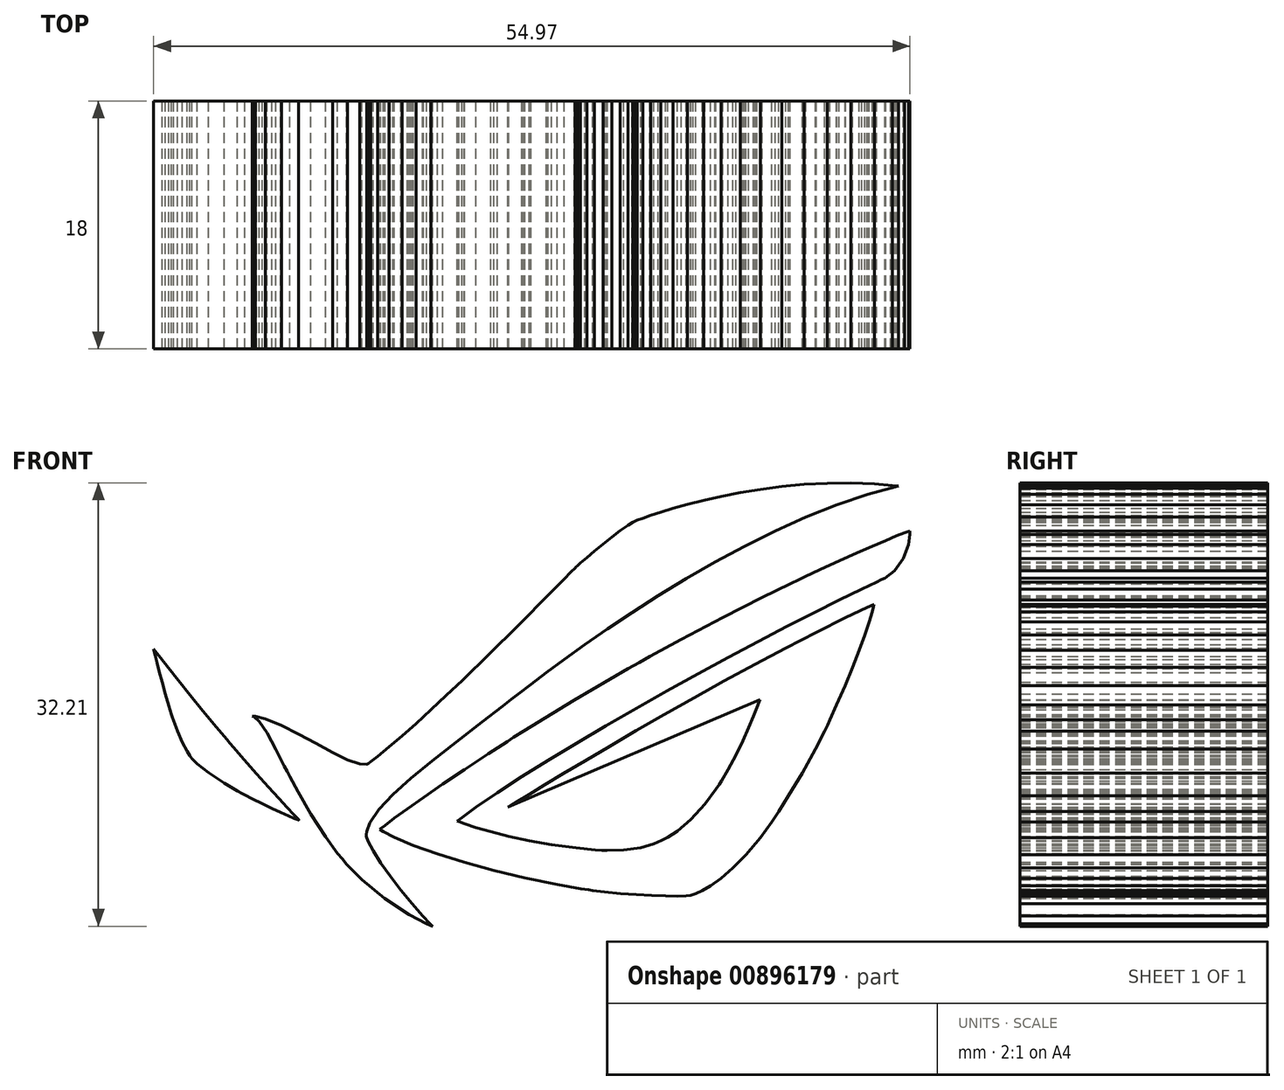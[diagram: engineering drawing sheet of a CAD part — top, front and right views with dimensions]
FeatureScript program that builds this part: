
annotation { "Feature Type Name" : "Feature", "Feature Type Description" : "" }
export const myFeature = defineFeature(function(context is Context, id is Id, definition is map)
    precondition{}
    {
        {
            var Q0;
            Q0=qCreatedBy(makeId("Front.planeOp"),FACE);
            var sketch = newSketch(context, id + "F0", { "sketchPlane" : qUnion([Q0])});
            skLineSegment(sketch, "E0", {"start": v(-0.13, -0.24) * mm, "end": v(-0.06, -0.2) * mm});
            skLineSegment(sketch, "E1", {"start": v(-0.06, -0.2) * mm, "end": v(0.3, 0.03) * mm});
            skLineSegment(sketch, "E2", {"start": v(0.3, 0.03) * mm, "end": v(0.7, 0.26) * mm});
            skLineSegment(sketch, "E3", {"start": v(0.7, 0.26) * mm, "end": v(0.78, 0.3) * mm});
            skLineSegment(sketch, "E4", {"start": v(0.78, 0.3) * mm, "end": v(0.86, 0.35) * mm});
            skLineSegment(sketch, "E5", {"start": v(0.86, 0.35) * mm, "end": v(1.09, 0.48) * mm});
            skLineSegment(sketch, "E6", {"start": v(1.09, 0.48) * mm, "end": v(1.39, 0.63) * mm});
            skLineSegment(sketch, "E7", {"start": v(1.39, 0.63) * mm, "end": v(1.68, 0.78) * mm});
            skLineSegment(sketch, "E8", {"start": v(1.68, 0.78) * mm, "end": v(1.88, 0.88) * mm});
            skLineSegment(sketch, "E9", {"start": v(1.88, 0.88) * mm, "end": v(1.94, 0.91) * mm});
            skLineSegment(sketch, "E10", {"start": v(1.94, 0.91) * mm, "end": v(1.98, 0.93) * mm});
            skLineSegment(sketch, "E11", {"start": v(1.98, 0.93) * mm, "end": v(2.1, 0.98) * mm});
            skLineSegment(sketch, "E12", {"start": v(2.1, 0.98) * mm, "end": v(2.23, 1.05) * mm});
            skLineSegment(sketch, "E13", {"start": v(2.23, 1.05) * mm, "end": v(2.36, 1.1) * mm});
            skLineSegment(sketch, "E14", {"start": v(2.36, 1.1) * mm, "end": v(2.47, 1.15) * mm});
            skLineSegment(sketch, "E15", {"start": v(2.47, 1.15) * mm, "end": v(2.57, 1.2) * mm});
            skLineSegment(sketch, "E16", {"start": v(2.57, 1.2) * mm, "end": v(2.65, 1.23) * mm});
            skLineSegment(sketch, "E17", {"start": v(2.65, 1.23) * mm, "end": v(2.7, 1.25) * mm});
            skLineSegment(sketch, "E18", {"start": v(2.7, 1.25) * mm, "end": v(2.74, 1.26) * mm});
            skLineSegment(sketch, "E19", {"start": v(2.74, 1.26) * mm, "end": v(2.75, 1.26) * mm});
            skLineSegment(sketch, "E20", {"start": v(2.75, 1.26) * mm, "end": v(2.75, 1.24) * mm});
            skLineSegment(sketch, "E21", {"start": v(2.75, 1.24) * mm, "end": v(2.74, 1.16) * mm});
            skLineSegment(sketch, "E22", {"start": v(2.74, 1.16) * mm, "end": v(2.7, 1.06) * mm});
            skLineSegment(sketch, "E23", {"start": v(2.7, 1.06) * mm, "end": v(2.63, 0.97) * mm});
            skLineSegment(sketch, "E24", {"start": v(2.63, 0.97) * mm, "end": v(2.57, 0.92) * mm});
            skLineSegment(sketch, "E25", {"start": v(2.57, 0.92) * mm, "end": v(2.54, 0.9) * mm});
            skLineSegment(sketch, "E26", {"start": v(2.54, 0.9) * mm, "end": v(2.5, 0.9) * mm});
            skLineSegment(sketch, "E27", {"start": v(2.5, 0.9) * mm, "end": v(2.4, 0.84) * mm});
            skLineSegment(sketch, "E28", {"start": v(2.4, 0.84) * mm, "end": v(2.23, 0.76) * mm});
            skLineSegment(sketch, "E29", {"start": v(2.23, 0.76) * mm, "end": v(2.05, 0.67) * mm});
            skLineSegment(sketch, "E30", {"start": v(2.05, 0.67) * mm, "end": v(1.85, 0.57) * mm});
            skLineSegment(sketch, "E31", {"start": v(1.85, 0.57) * mm, "end": v(1.65, 0.46) * mm});
            skLineSegment(sketch, "E32", {"start": v(1.65, 0.46) * mm, "end": v(1.43, 0.34) * mm});
            skLineSegment(sketch, "E33", {"start": v(1.43, 0.34) * mm, "end": v(1.2, 0.22) * mm});
            skLineSegment(sketch, "E34", {"start": v(1.2, 0.22) * mm, "end": v(0.98, 0.1) * mm});
            skLineSegment(sketch, "E35", {"start": v(0.98, 0.1) * mm, "end": v(0.76, -0.03) * mm});
            skLineSegment(sketch, "E36", {"start": v(0.76, -0.03) * mm, "end": v(0.54, -0.15) * mm});
            skLineSegment(sketch, "E37", {"start": v(0.54, -0.15) * mm, "end": v(0.32, -0.28) * mm});
            skLineSegment(sketch, "E38", {"start": v(0.32, -0.28) * mm, "end": v(0.12, -0.4) * mm});
            skLineSegment(sketch, "E39", {"start": v(0.12, -0.4) * mm, "end": v(-0.07, -0.52) * mm});
            skLineSegment(sketch, "E40", {"start": v(-0.07, -0.52) * mm, "end": v(-0.25, -0.64) * mm});
            skLineSegment(sketch, "E41", {"start": v(-0.25, -0.64) * mm, "end": v(-0.4, -0.75) * mm});
            skLineSegment(sketch, "E42", {"start": v(-0.4, -0.75) * mm, "end": v(-0.5, -0.82) * mm});
            skLineSegment(sketch, "E43", {"start": v(-0.5, -0.82) * mm, "end": v(-0.54, -0.85) * mm});
            skLineSegment(sketch, "E44", {"start": v(-0.54, -0.85) * mm, "end": v(-0.53, -0.85) * mm});
            skLineSegment(sketch, "E45", {"start": v(-0.53, -0.85) * mm, "end": v(-0.49, -0.87) * mm});
            skLineSegment(sketch, "E46", {"start": v(-0.49, -0.87) * mm, "end": v(-0.4, -0.9) * mm});
            skLineSegment(sketch, "E47", {"start": v(-0.4, -0.9) * mm, "end": v(-0.3, -0.92) * mm});
            skLineSegment(sketch, "E48", {"start": v(-0.3, -0.92) * mm, "end": v(-0.17, -0.96) * mm});
            skLineSegment(sketch, "E49", {"start": v(-0.17, -0.96) * mm, "end": v(-0.02, -0.99) * mm});
            skLineSegment(sketch, "E50", {"start": v(-0.02, -0.99) * mm, "end": v(0.14, -1.02) * mm});
            skLineSegment(sketch, "E51", {"start": v(0.14, -1.02) * mm, "end": v(0.32, -1.04) * mm});
            skLineSegment(sketch, "E52", {"start": v(0.32, -1.04) * mm, "end": v(0.46, -1.05) * mm});
            skLineSegment(sketch, "E53", {"start": v(0.46, -1.05) * mm, "end": v(0.5, -1.06) * mm});
            skLineSegment(sketch, "E54", {"start": v(0.5, -1.06) * mm, "end": v(0.55, -1.06) * mm});
            skLineSegment(sketch, "E55", {"start": v(0.55, -1.06) * mm, "end": v(0.67, -1.06) * mm});
            skLineSegment(sketch, "E56", {"start": v(0.67, -1.06) * mm, "end": v(0.8, -1.04) * mm});
            skLineSegment(sketch, "E57", {"start": v(0.8, -1.04) * mm, "end": v(0.89, -1.01) * mm});
            skLineSegment(sketch, "E58", {"start": v(0.89, -1.01) * mm, "end": v(0.94, -0.99) * mm});
            skLineSegment(sketch, "E59", {"start": v(0.94, -0.99) * mm, "end": v(0.96, -0.98) * mm});
            skLineSegment(sketch, "E60", {"start": v(0.96, -0.98) * mm, "end": v(0.99, -0.97) * mm});
            skLineSegment(sketch, "E61", {"start": v(0.99, -0.97) * mm, "end": v(1.06, -0.92) * mm});
            skLineSegment(sketch, "E62", {"start": v(1.06, -0.92) * mm, "end": v(1.16, -0.83) * mm});
            skLineSegment(sketch, "E63", {"start": v(1.16, -0.83) * mm, "end": v(1.26, -0.72) * mm});
            skLineSegment(sketch, "E64", {"start": v(1.26, -0.72) * mm, "end": v(1.34, -0.62) * mm});
            skLineSegment(sketch, "E65", {"start": v(1.34, -0.62) * mm, "end": v(1.36, -0.58) * mm});
            skLineSegment(sketch, "E66", {"start": v(1.36, -0.58) * mm, "end": v(1.38, -0.55) * mm});
            skLineSegment(sketch, "E67", {"start": v(1.38, -0.55) * mm, "end": v(1.43, -0.47) * mm});
            skLineSegment(sketch, "E68", {"start": v(1.43, -0.47) * mm, "end": v(1.48, -0.37) * mm});
            skLineSegment(sketch, "E69", {"start": v(1.48, -0.37) * mm, "end": v(1.53, -0.26) * mm});
            skLineSegment(sketch, "E70", {"start": v(1.53, -0.26) * mm, "end": v(1.58, -0.17) * mm});
            skLineSegment(sketch, "E71", {"start": v(1.58, -0.17) * mm, "end": v(1.61, -0.08) * mm});
            skLineSegment(sketch, "E72", {"start": v(1.61, -0.08) * mm, "end": v(1.64, -0.02) * mm});
            skLineSegment(sketch, "E73", {"start": v(1.64, -0.02) * mm, "end": v(1.65, 0.02) * mm});
            skLineSegment(sketch, "E74", {"start": v(1.65, 0.02) * mm, "end": v(1.66, 0.04) * mm});
            skLineSegment(sketch, "E75", {"start": v(1.66, 0.04) * mm, "end": v(-0.17, -0.75) * mm});
            skLineSegment(sketch, "E76", {"start": v(-0.17, -0.75) * mm, "end": v(-0.16, -0.73) * mm});
            skLineSegment(sketch, "E77", {"start": v(-0.16, -0.73) * mm, "end": v(-0.1, -0.7) * mm});
            skLineSegment(sketch, "E78", {"start": v(-0.1, -0.7) * mm, "end": v(-0.02, -0.65) * mm});
            skLineSegment(sketch, "E79", {"start": v(-0.02, -0.65) * mm, "end": v(0.1, -0.58) * mm});
            skLineSegment(sketch, "E80", {"start": v(0.1, -0.58) * mm, "end": v(0.23, -0.5) * mm});
            skLineSegment(sketch, "E81", {"start": v(0.23, -0.5) * mm, "end": v(0.39, -0.4) * mm});
            skLineSegment(sketch, "E82", {"start": v(0.39, -0.4) * mm, "end": v(0.56, -0.3) * mm});
            skLineSegment(sketch, "E83", {"start": v(0.56, -0.3) * mm, "end": v(0.76, -0.2) * mm});
            skLineSegment(sketch, "E84", {"start": v(0.76, -0.2) * mm, "end": v(0.96, -0.07) * mm});
            skLineSegment(sketch, "E85", {"start": v(0.96, -0.07) * mm, "end": v(1.18, 0.05) * mm});
            skLineSegment(sketch, "E86", {"start": v(1.18, 0.05) * mm, "end": v(1.4, 0.17) * mm});
            skLineSegment(sketch, "E87", {"start": v(1.4, 0.17) * mm, "end": v(1.62, 0.3) * mm});
            skLineSegment(sketch, "E88", {"start": v(1.62, 0.3) * mm, "end": v(1.85, 0.41) * mm});
            skLineSegment(sketch, "E89", {"start": v(1.85, 0.41) * mm, "end": v(2.07, 0.53) * mm});
            skLineSegment(sketch, "E90", {"start": v(2.07, 0.53) * mm, "end": v(2.28, 0.63) * mm});
            skLineSegment(sketch, "E91", {"start": v(2.28, 0.63) * mm, "end": v(2.43, 0.7) * mm});
            skLineSegment(sketch, "E92", {"start": v(2.43, 0.7) * mm, "end": v(2.49, 0.73) * mm});
            skLineSegment(sketch, "E93", {"start": v(2.49, 0.73) * mm, "end": v(2.48, 0.72) * mm});
            skLineSegment(sketch, "E94", {"start": v(2.48, 0.72) * mm, "end": v(2.47, 0.68) * mm});
            skLineSegment(sketch, "E95", {"start": v(2.47, 0.68) * mm, "end": v(2.45, 0.6) * mm});
            skLineSegment(sketch, "E96", {"start": v(2.45, 0.6) * mm, "end": v(2.42, 0.5) * mm});
            skLineSegment(sketch, "E97", {"start": v(2.42, 0.5) * mm, "end": v(2.38, 0.4) * mm});
            skLineSegment(sketch, "E98", {"start": v(2.38, 0.4) * mm, "end": v(2.33, 0.27) * mm});
            skLineSegment(sketch, "E99", {"start": v(2.33, 0.27) * mm, "end": v(2.28, 0.14) * mm});
            skLineSegment(sketch, "E100", {"start": v(2.28, 0.14) * mm, "end": v(2.22, 0) * mm});
            skLineSegment(sketch, "E101", {"start": v(2.22, 0) * mm, "end": v(2.17, -0.11) * mm});
            skLineSegment(sketch, "E102", {"start": v(2.17, -0.11) * mm, "end": v(2.15, -0.15) * mm});
            skLineSegment(sketch, "E103", {"start": v(2.15, -0.15) * mm, "end": v(2.13, -0.2) * mm});
            skLineSegment(sketch, "E104", {"start": v(2.13, -0.2) * mm, "end": v(2.06, -0.32) * mm});
            skLineSegment(sketch, "E105", {"start": v(2.06, -0.32) * mm, "end": v(1.96, -0.5) * mm});
            skLineSegment(sketch, "E106", {"start": v(1.96, -0.5) * mm, "end": v(1.87, -0.66) * mm});
            skLineSegment(sketch, "E107", {"start": v(1.87, -0.66) * mm, "end": v(1.8, -0.78) * mm});
            skLineSegment(sketch, "E108", {"start": v(1.8, -0.78) * mm, "end": v(1.77, -0.81) * mm});
            skLineSegment(sketch, "E109", {"start": v(1.77, -0.81) * mm, "end": v(1.74, -0.85) * mm});
            skLineSegment(sketch, "E110", {"start": v(1.74, -0.85) * mm, "end": v(1.66, -0.97) * mm});
            skLineSegment(sketch, "E111", {"start": v(1.66, -0.97) * mm, "end": v(1.56, -1.1) * mm});
            skLineSegment(sketch, "E112", {"start": v(1.56, -1.1) * mm, "end": v(1.46, -1.19) * mm});
            skLineSegment(sketch, "E113", {"start": v(1.46, -1.19) * mm, "end": v(1.37, -1.26) * mm});
            skLineSegment(sketch, "E114", {"start": v(1.37, -1.26) * mm, "end": v(1.3, -1.31) * mm});
            skLineSegment(sketch, "E115", {"start": v(1.3, -1.31) * mm, "end": v(1.24, -1.35) * mm});
            skLineSegment(sketch, "E116", {"start": v(1.24, -1.35) * mm, "end": v(1.2, -1.37) * mm});
            skLineSegment(sketch, "E117", {"start": v(1.2, -1.37) * mm, "end": v(1.17, -1.38) * mm});
            skLineSegment(sketch, "E118", {"start": v(1.17, -1.38) * mm, "end": v(1.16, -1.38) * mm});
            skLineSegment(sketch, "E119", {"start": v(1.16, -1.38) * mm, "end": v(1.15, -1.38) * mm});
            skLineSegment(sketch, "E120", {"start": v(1.15, -1.38) * mm, "end": v(1.12, -1.39) * mm});
            skLineSegment(sketch, "E121", {"start": v(1.12, -1.39) * mm, "end": v(1.06, -1.4) * mm});
            skLineSegment(sketch, "E122", {"start": v(1.06, -1.4) * mm, "end": v(0.97, -1.4) * mm});
            skLineSegment(sketch, "E123", {"start": v(0.97, -1.4) * mm, "end": v(0.87, -1.39) * mm});
            skLineSegment(sketch, "E124", {"start": v(0.87, -1.39) * mm, "end": v(0.76, -1.38) * mm});
            skLineSegment(sketch, "E125", {"start": v(0.76, -1.38) * mm, "end": v(0.64, -1.37) * mm});
            skLineSegment(sketch, "E126", {"start": v(0.64, -1.37) * mm, "end": v(0.53, -1.36) * mm});
            skLineSegment(sketch, "E127", {"start": v(0.53, -1.36) * mm, "end": v(0.44, -1.35) * mm});
            skLineSegment(sketch, "E128", {"start": v(0.44, -1.35) * mm, "end": v(0.41, -1.35) * mm});
            skLineSegment(sketch, "E129", {"start": v(0.41, -1.35) * mm, "end": v(0.36, -1.34) * mm});
            skLineSegment(sketch, "E130", {"start": v(0.36, -1.34) * mm, "end": v(0.18, -1.3) * mm});
            skLineSegment(sketch, "E131", {"start": v(0.18, -1.3) * mm, "end": v(-0.05, -1.26) * mm});
            skLineSegment(sketch, "E132", {"start": v(-0.05, -1.26) * mm, "end": v(-0.28, -1.2) * mm});
            skLineSegment(sketch, "E133", {"start": v(-0.28, -1.2) * mm, "end": v(-0.5, -1.15) * mm});
            skLineSegment(sketch, "E134", {"start": v(-0.5, -1.15) * mm, "end": v(-0.69, -1.08) * mm});
            skLineSegment(sketch, "E135", {"start": v(-0.69, -1.08) * mm, "end": v(-0.86, -1.02) * mm});
            skLineSegment(sketch, "E136", {"start": v(-0.86, -1.02) * mm, "end": v(-1, -0.96) * mm});
            skLineSegment(sketch, "E137", {"start": v(-1, -0.96) * mm, "end": v(-1.08, -0.92) * mm});
            skLineSegment(sketch, "E138", {"start": v(-1.08, -0.92) * mm, "end": v(-1.1, -0.9) * mm});
            skLineSegment(sketch, "E139", {"start": v(-1.1, -0.9) * mm, "end": v(-1.1, -0.9) * mm});
            skLineSegment(sketch, "E140", {"start": v(-1.1, -0.9) * mm, "end": v(-1.07, -0.88) * mm});
            skLineSegment(sketch, "E141", {"start": v(-1.07, -0.88) * mm, "end": v(-1, -0.83) * mm});
            skLineSegment(sketch, "E142", {"start": v(-1, -0.83) * mm, "end": v(-0.9, -0.76) * mm});
            skLineSegment(sketch, "E143", {"start": v(-0.9, -0.76) * mm, "end": v(-0.79, -0.67) * mm});
            skLineSegment(sketch, "E144", {"start": v(-0.79, -0.67) * mm, "end": v(-0.65, -0.58) * mm});
            skLineSegment(sketch, "E145", {"start": v(-0.65, -0.58) * mm, "end": v(-0.49, -0.47) * mm});
            skLineSegment(sketch, "E146", {"start": v(-0.49, -0.47) * mm, "end": v(-0.32, -0.36) * mm});
            skLineSegment(sketch, "E147", {"start": v(-0.32, -0.36) * mm, "end": v(-0.18, -0.27) * mm});
            skLineSegment(sketch, "E148", {"start": v(-0.18, -0.27) * mm, "end": v(-0.13, -0.24) * mm});
            skLineSegment(sketch, "E149", {"start": v(-2.1, -0.65) * mm, "end": v(-2.14, -0.63) * mm});
            skLineSegment(sketch, "E150", {"start": v(-2.14, -0.63) * mm, "end": v(-2.24, -0.57) * mm});
            skLineSegment(sketch, "E151", {"start": v(-2.24, -0.57) * mm, "end": v(-2.35, -0.5) * mm});
            skLineSegment(sketch, "E152", {"start": v(-2.35, -0.5) * mm, "end": v(-2.43, -0.43) * mm});
            skLineSegment(sketch, "E153", {"start": v(-2.43, -0.43) * mm, "end": v(-2.47, -0.4) * mm});
            skLineSegment(sketch, "E154", {"start": v(-2.47, -0.4) * mm, "end": v(-2.48, -0.38) * mm});
            skLineSegment(sketch, "E155", {"start": v(-2.48, -0.38) * mm, "end": v(-2.49, -0.37) * mm});
            skLineSegment(sketch, "E156", {"start": v(-2.49, -0.37) * mm, "end": v(-2.5, -0.34) * mm});
            skLineSegment(sketch, "E157", {"start": v(-2.5, -0.34) * mm, "end": v(-2.54, -0.28) * mm});
            skLineSegment(sketch, "E158", {"start": v(-2.54, -0.28) * mm, "end": v(-2.57, -0.2) * mm});
            skLineSegment(sketch, "E159", {"start": v(-2.57, -0.2) * mm, "end": v(-2.6, -0.12) * mm});
            skLineSegment(sketch, "E160", {"start": v(-2.6, -0.12) * mm, "end": v(-2.61, -0.1) * mm});
            skLineSegment(sketch, "E161", {"start": v(-2.61, -0.1) * mm, "end": v(-2.62, -0.07) * mm});
            skLineSegment(sketch, "E162", {"start": v(-2.62, -0.07) * mm, "end": v(-2.64, 0) * mm});
            skLineSegment(sketch, "E163", {"start": v(-2.64, 0) * mm, "end": v(-2.66, 0.08) * mm});
            skLineSegment(sketch, "E164", {"start": v(-2.66, 0.08) * mm, "end": v(-2.69, 0.16) * mm});
            skLineSegment(sketch, "E165", {"start": v(-2.69, 0.16) * mm, "end": v(-2.7, 0.24) * mm});
            skLineSegment(sketch, "E166", {"start": v(-2.7, 0.24) * mm, "end": v(-2.72, 0.3) * mm});
            skLineSegment(sketch, "E167", {"start": v(-2.72, 0.3) * mm, "end": v(-2.74, 0.36) * mm});
            skLineSegment(sketch, "E168", {"start": v(-2.74, 0.36) * mm, "end": v(-2.75, 0.4) * mm});
            skLineSegment(sketch, "E169", {"start": v(-2.75, 0.4) * mm, "end": v(-2.75, 0.4) * mm});
            skLineSegment(sketch, "E170", {"start": v(-2.75, 0.4) * mm, "end": v(-2.73, 0.39) * mm});
            skLineSegment(sketch, "E171", {"start": v(-2.73, 0.39) * mm, "end": v(-2.7, 0.34) * mm});
            skLineSegment(sketch, "E172", {"start": v(-2.7, 0.34) * mm, "end": v(-2.64, 0.27) * mm});
            skLineSegment(sketch, "E173", {"start": v(-2.64, 0.27) * mm, "end": v(-2.57, 0.18) * mm});
            skLineSegment(sketch, "E174", {"start": v(-2.57, 0.18) * mm, "end": v(-2.48, 0.07) * mm});
            skLineSegment(sketch, "E175", {"start": v(-2.48, 0.07) * mm, "end": v(-2.39, -0.05) * mm});
            skLineSegment(sketch, "E176", {"start": v(-2.39, -0.05) * mm, "end": v(-2.3, -0.17) * mm});
            skLineSegment(sketch, "E177", {"start": v(-2.3, -0.17) * mm, "end": v(-2.22, -0.25) * mm});
            skLineSegment(sketch, "E178", {"start": v(-2.22, -0.25) * mm, "end": v(-2.2, -0.28) * mm});
            skLineSegment(sketch, "E179", {"start": v(-2.2, -0.28) * mm, "end": v(-2.17, -0.31) * mm});
            skLineSegment(sketch, "E180", {"start": v(-2.17, -0.31) * mm, "end": v(-2.1, -0.4) * mm});
            skLineSegment(sketch, "E181", {"start": v(-2.1, -0.4) * mm, "end": v(-2, -0.5) * mm});
            skLineSegment(sketch, "E182", {"start": v(-2, -0.5) * mm, "end": v(-1.91, -0.6) * mm});
            skLineSegment(sketch, "E183", {"start": v(-1.91, -0.6) * mm, "end": v(-1.84, -0.68) * mm});
            skLineSegment(sketch, "E184", {"start": v(-1.84, -0.68) * mm, "end": v(-1.78, -0.75) * mm});
            skLineSegment(sketch, "E185", {"start": v(-1.78, -0.75) * mm, "end": v(-1.73, -0.8) * mm});
            skLineSegment(sketch, "E186", {"start": v(-1.73, -0.8) * mm, "end": v(-1.7, -0.83) * mm});
            skLineSegment(sketch, "E187", {"start": v(-1.7, -0.83) * mm, "end": v(-1.69, -0.84) * mm});
            skLineSegment(sketch, "E188", {"start": v(-1.69, -0.84) * mm, "end": v(-1.7, -0.84) * mm});
            skLineSegment(sketch, "E189", {"start": v(-1.7, -0.84) * mm, "end": v(-1.73, -0.83) * mm});
            skLineSegment(sketch, "E190", {"start": v(-1.73, -0.83) * mm, "end": v(-1.77, -0.8) * mm});
            skLineSegment(sketch, "E191", {"start": v(-1.77, -0.8) * mm, "end": v(-1.82, -0.78) * mm});
            skLineSegment(sketch, "E192", {"start": v(-1.82, -0.78) * mm, "end": v(-1.89, -0.75) * mm});
            skLineSegment(sketch, "E193", {"start": v(-1.89, -0.75) * mm, "end": v(-1.96, -0.72) * mm});
            skLineSegment(sketch, "E194", {"start": v(-1.96, -0.72) * mm, "end": v(-2.03, -0.68) * mm});
            skLineSegment(sketch, "E195", {"start": v(-2.03, -0.68) * mm, "end": v(-2.09, -0.66) * mm});
            skLineSegment(sketch, "E196", {"start": v(-2.09, -0.66) * mm, "end": v(-2.1, -0.65) * mm});
            skLineSegment(sketch, "E197", {"start": v(-0.16, 0.03) * mm, "end": v(-0.21, -0.01) * mm});
            skLineSegment(sketch, "E198", {"start": v(-0.21, -0.01) * mm, "end": v(-0.36, -0.13) * mm});
            skLineSegment(sketch, "E199", {"start": v(-0.36, -0.13) * mm, "end": v(-0.55, -0.27) * mm});
            skLineSegment(sketch, "E200", {"start": v(-0.55, -0.27) * mm, "end": v(-0.72, -0.4) * mm});
            skLineSegment(sketch, "E201", {"start": v(-0.72, -0.4) * mm, "end": v(-0.88, -0.53) * mm});
            skLineSegment(sketch, "E202", {"start": v(-0.88, -0.53) * mm, "end": v(-1, -0.65) * mm});
            skLineSegment(sketch, "E203", {"start": v(-1, -0.65) * mm, "end": v(-1.11, -0.76) * mm});
            skLineSegment(sketch, "E204", {"start": v(-1.11, -0.76) * mm, "end": v(-1.18, -0.86) * mm});
            skLineSegment(sketch, "E205", {"start": v(-1.18, -0.86) * mm, "end": v(-1.2, -0.92) * mm});
            skLineSegment(sketch, "E206", {"start": v(-1.2, -0.92) * mm, "end": v(-1.2, -0.94) * mm});
            skLineSegment(sketch, "E207", {"start": v(-1.2, -0.94) * mm, "end": v(-1.2, -0.96) * mm});
            skLineSegment(sketch, "E208", {"start": v(-1.2, -0.96) * mm, "end": v(-1.19, -1) * mm});
            skLineSegment(sketch, "E209", {"start": v(-1.19, -1) * mm, "end": v(-1.15, -1.06) * mm});
            skLineSegment(sketch, "E210", {"start": v(-1.15, -1.06) * mm, "end": v(-1.1, -1.15) * mm});
            skLineSegment(sketch, "E211", {"start": v(-1.1, -1.15) * mm, "end": v(-1.03, -1.25) * mm});
            skLineSegment(sketch, "E212", {"start": v(-1.03, -1.25) * mm, "end": v(-0.95, -1.35) * mm});
            skLineSegment(sketch, "E213", {"start": v(-0.95, -1.35) * mm, "end": v(-0.87, -1.45) * mm});
            skLineSegment(sketch, "E214", {"start": v(-0.87, -1.45) * mm, "end": v(-0.8, -1.54) * mm});
            skLineSegment(sketch, "E215", {"start": v(-0.8, -1.54) * mm, "end": v(-0.74, -1.6) * mm});
            skLineSegment(sketch, "E216", {"start": v(-0.74, -1.6) * mm, "end": v(-0.72, -1.61) * mm});
            skLineSegment(sketch, "E217", {"start": v(-0.72, -1.61) * mm, "end": v(-0.77, -1.6) * mm});
            skLineSegment(sketch, "E218", {"start": v(-0.77, -1.6) * mm, "end": v(-0.9, -1.52) * mm});
            skLineSegment(sketch, "E219", {"start": v(-0.9, -1.52) * mm, "end": v(-1.07, -1.4) * mm});
            skLineSegment(sketch, "E220", {"start": v(-1.07, -1.4) * mm, "end": v(-1.23, -1.27) * mm});
            skLineSegment(sketch, "E221", {"start": v(-1.23, -1.27) * mm, "end": v(-1.35, -1.16) * mm});
            skLineSegment(sketch, "E222", {"start": v(-1.35, -1.16) * mm, "end": v(-1.38, -1.12) * mm});
            skLineSegment(sketch, "E223", {"start": v(-1.38, -1.12) * mm, "end": v(-1.41, -1.08) * mm});
            skLineSegment(sketch, "E224", {"start": v(-1.41, -1.08) * mm, "end": v(-1.5, -0.96) * mm});
            skLineSegment(sketch, "E225", {"start": v(-1.5, -0.96) * mm, "end": v(-1.6, -0.8) * mm});
            skLineSegment(sketch, "E226", {"start": v(-1.6, -0.8) * mm, "end": v(-1.7, -0.63) * mm});
            skLineSegment(sketch, "E227", {"start": v(-1.7, -0.63) * mm, "end": v(-1.76, -0.52) * mm});
            skLineSegment(sketch, "E228", {"start": v(-1.76, -0.52) * mm, "end": v(-1.78, -0.49) * mm});
            skLineSegment(sketch, "E229", {"start": v(-1.78, -0.49) * mm, "end": v(-1.8, -0.45) * mm});
            skLineSegment(sketch, "E230", {"start": v(-1.8, -0.45) * mm, "end": v(-1.86, -0.33) * mm});
            skLineSegment(sketch, "E231", {"start": v(-1.86, -0.33) * mm, "end": v(-1.92, -0.2) * mm});
            skLineSegment(sketch, "E232", {"start": v(-1.92, -0.2) * mm, "end": v(-1.98, -0.12) * mm});
            skLineSegment(sketch, "E233", {"start": v(-1.98, -0.12) * mm, "end": v(-2.02, -0.09) * mm});
            skLineSegment(sketch, "E234", {"start": v(-2.02, -0.09) * mm, "end": v(-2.03, -0.08) * mm});
            skLineSegment(sketch, "E235", {"start": v(-2.03, -0.08) * mm, "end": v(-2, -0.08) * mm});
            skLineSegment(sketch, "E236", {"start": v(-2, -0.08) * mm, "end": v(-1.93, -0.1) * mm});
            skLineSegment(sketch, "E237", {"start": v(-1.93, -0.1) * mm, "end": v(-1.82, -0.15) * mm});
            skLineSegment(sketch, "E238", {"start": v(-1.82, -0.15) * mm, "end": v(-1.7, -0.21) * mm});
            skLineSegment(sketch, "E239", {"start": v(-1.7, -0.21) * mm, "end": v(-1.57, -0.28) * mm});
            skLineSegment(sketch, "E240", {"start": v(-1.57, -0.28) * mm, "end": v(-1.45, -0.35) * mm});
            skLineSegment(sketch, "E241", {"start": v(-1.45, -0.35) * mm, "end": v(-1.34, -0.4) * mm});
            skLineSegment(sketch, "E242", {"start": v(-1.34, -0.4) * mm, "end": v(-1.25, -0.43) * mm});
            skLineSegment(sketch, "E243", {"start": v(-1.25, -0.43) * mm, "end": v(-1.2, -0.43) * mm});
            skLineSegment(sketch, "E244", {"start": v(-1.2, -0.43) * mm, "end": v(-1.19, -0.43) * mm});
            skLineSegment(sketch, "E245", {"start": v(-1.19, -0.43) * mm, "end": v(-1.17, -0.42) * mm});
            skLineSegment(sketch, "E246", {"start": v(-1.17, -0.42) * mm, "end": v(-1.12, -0.38) * mm});
            skLineSegment(sketch, "E247", {"start": v(-1.12, -0.38) * mm, "end": v(-1.04, -0.3) * mm});
            skLineSegment(sketch, "E248", {"start": v(-1.04, -0.3) * mm, "end": v(-0.94, -0.23) * mm});
            skLineSegment(sketch, "E249", {"start": v(-0.94, -0.23) * mm, "end": v(-0.84, -0.14) * mm});
            skLineSegment(sketch, "E250", {"start": v(-0.84, -0.14) * mm, "end": v(-0.73, -0.04) * mm});
            skLineSegment(sketch, "E251", {"start": v(-0.73, -0.04) * mm, "end": v(-0.62, 0.07) * mm});
            skLineSegment(sketch, "E252", {"start": v(-0.62, 0.07) * mm, "end": v(-0.5, 0.18) * mm});
            skLineSegment(sketch, "E253", {"start": v(-0.5, 0.18) * mm, "end": v(-0.42, 0.26) * mm});
            skLineSegment(sketch, "E254", {"start": v(-0.42, 0.26) * mm, "end": v(-0.39, 0.29) * mm});
            skLineSegment(sketch, "E255", {"start": v(-0.39, 0.29) * mm, "end": v(-0.36, 0.32) * mm});
            skLineSegment(sketch, "E256", {"start": v(-0.36, 0.32) * mm, "end": v(-0.27, 0.41) * mm});
            skLineSegment(sketch, "E257", {"start": v(-0.27, 0.41) * mm, "end": v(-0.15, 0.53) * mm});
            skLineSegment(sketch, "E258", {"start": v(-0.15, 0.53) * mm, "end": v(-0.03, 0.64) * mm});
            skLineSegment(sketch, "E259", {"start": v(-0.03, 0.64) * mm, "end": v(0.07, 0.74) * mm});
            skLineSegment(sketch, "E260", {"start": v(0.07, 0.74) * mm, "end": v(0.16, 0.83) * mm});
            skLineSegment(sketch, "E261", {"start": v(0.16, 0.83) * mm, "end": v(0.23, 0.9) * mm});
            skLineSegment(sketch, "E262", {"start": v(0.23, 0.9) * mm, "end": v(0.29, 0.97) * mm});
            skLineSegment(sketch, "E263", {"start": v(0.29, 0.97) * mm, "end": v(0.31, 1) * mm});
            skLineSegment(sketch, "E264", {"start": v(0.31, 1) * mm, "end": v(0.32, 1) * mm});
            skLineSegment(sketch, "E265", {"start": v(0.32, 1) * mm, "end": v(0.33, 1) * mm});
            skLineSegment(sketch, "E266", {"start": v(0.33, 1) * mm, "end": v(0.35, 1.03) * mm});
            skLineSegment(sketch, "E267", {"start": v(0.35, 1.03) * mm, "end": v(0.4, 1.07) * mm});
            skLineSegment(sketch, "E268", {"start": v(0.4, 1.07) * mm, "end": v(0.46, 1.12) * mm});
            skLineSegment(sketch, "E269", {"start": v(0.46, 1.12) * mm, "end": v(0.52, 1.17) * mm});
            skLineSegment(sketch, "E270", {"start": v(0.52, 1.17) * mm, "end": v(0.58, 1.22) * mm});
            skLineSegment(sketch, "E271", {"start": v(0.58, 1.22) * mm, "end": v(0.64, 1.26) * mm});
            skLineSegment(sketch, "E272", {"start": v(0.64, 1.26) * mm, "end": v(0.7, 1.3) * mm});
            skLineSegment(sketch, "E273", {"start": v(0.7, 1.3) * mm, "end": v(0.73, 1.33) * mm});
            skLineSegment(sketch, "E274", {"start": v(0.73, 1.33) * mm, "end": v(0.75, 1.33) * mm});
            skLineSegment(sketch, "E275", {"start": v(0.75, 1.33) * mm, "end": v(0.75, 1.33) * mm});
            skLineSegment(sketch, "E276", {"start": v(0.75, 1.33) * mm, "end": v(0.77, 1.34) * mm});
            skLineSegment(sketch, "E277", {"start": v(0.77, 1.34) * mm, "end": v(0.8, 1.35) * mm});
            skLineSegment(sketch, "E278", {"start": v(0.8, 1.35) * mm, "end": v(0.86, 1.37) * mm});
            skLineSegment(sketch, "E279", {"start": v(0.86, 1.37) * mm, "end": v(0.94, 1.4) * mm});
            skLineSegment(sketch, "E280", {"start": v(0.94, 1.4) * mm, "end": v(1.03, 1.43) * mm});
            skLineSegment(sketch, "E281", {"start": v(1.03, 1.43) * mm, "end": v(1.13, 1.45) * mm});
            skLineSegment(sketch, "E282", {"start": v(1.13, 1.45) * mm, "end": v(1.25, 1.48) * mm});
            skLineSegment(sketch, "E283", {"start": v(1.25, 1.48) * mm, "end": v(1.38, 1.51) * mm});
            skLineSegment(sketch, "E284", {"start": v(1.38, 1.51) * mm, "end": v(1.51, 1.54) * mm});
            skLineSegment(sketch, "E285", {"start": v(1.51, 1.54) * mm, "end": v(1.66, 1.56) * mm});
            skLineSegment(sketch, "E286", {"start": v(1.66, 1.56) * mm, "end": v(1.82, 1.58) * mm});
            skLineSegment(sketch, "E287", {"start": v(1.82, 1.58) * mm, "end": v(1.98, 1.6) * mm});
            skLineSegment(sketch, "E288", {"start": v(1.98, 1.6) * mm, "end": v(2.15, 1.6) * mm});
            skLineSegment(sketch, "E289", {"start": v(2.15, 1.6) * mm, "end": v(2.32, 1.61) * mm});
            skLineSegment(sketch, "E290", {"start": v(2.32, 1.61) * mm, "end": v(2.5, 1.6) * mm});
            skLineSegment(sketch, "E291", {"start": v(2.5, 1.6) * mm, "end": v(2.62, 1.6) * mm});
            skLineSegment(sketch, "E292", {"start": v(2.62, 1.6) * mm, "end": v(2.66, 1.59) * mm});
            skLineSegment(sketch, "E293", {"start": v(2.66, 1.59) * mm, "end": v(2.6, 1.57) * mm});
            skLineSegment(sketch, "E294", {"start": v(2.6, 1.57) * mm, "end": v(2.44, 1.53) * mm});
            skLineSegment(sketch, "E295", {"start": v(2.44, 1.53) * mm, "end": v(2.22, 1.45) * mm});
            skLineSegment(sketch, "E296", {"start": v(2.22, 1.45) * mm, "end": v(2, 1.36) * mm});
            skLineSegment(sketch, "E297", {"start": v(2, 1.36) * mm, "end": v(1.77, 1.26) * mm});
            skLineSegment(sketch, "E298", {"start": v(1.77, 1.26) * mm, "end": v(1.55, 1.15) * mm});
            skLineSegment(sketch, "E299", {"start": v(1.55, 1.15) * mm, "end": v(1.33, 1.04) * mm});
            skLineSegment(sketch, "E300", {"start": v(1.33, 1.04) * mm, "end": v(1.12, 0.91) * mm});
            skLineSegment(sketch, "E301", {"start": v(1.12, 0.91) * mm, "end": v(0.92, 0.8) * mm});
            skLineSegment(sketch, "E302", {"start": v(0.92, 0.8) * mm, "end": v(0.73, 0.67) * mm});
            skLineSegment(sketch, "E303", {"start": v(0.73, 0.67) * mm, "end": v(0.55, 0.55) * mm});
            skLineSegment(sketch, "E304", {"start": v(0.55, 0.55) * mm, "end": v(0.38, 0.44) * mm});
            skLineSegment(sketch, "E305", {"start": v(0.38, 0.44) * mm, "end": v(0.24, 0.33) * mm});
            skLineSegment(sketch, "E306", {"start": v(0.24, 0.33) * mm, "end": v(0.1, 0.23) * mm});
            skLineSegment(sketch, "E307", {"start": v(0.1, 0.23) * mm, "end": v(0, 0.15) * mm});
            skLineSegment(sketch, "E308", {"start": v(0, 0.15) * mm, "end": v(-0.1, 0.08) * mm});
            skLineSegment(sketch, "E309", {"start": v(-0.1, 0.08) * mm, "end": v(-0.15, 0.04) * mm});
            skLineSegment(sketch, "E310", {"start": v(-0.15, 0.04) * mm, "end": v(-0.16, 0.03) * mm});
            skSolve(sketch);
        }
        {
            var Q0;
            Q0=makeQuery(id+"F0.imprint","IMPRINT",FACE,{"disambiguationData":[TD([[makeQuery(id+"F0.imprint","IMPRINT",EDGE,{"derivedFrom":sQuery(id+"F0.wireOp",EDGE,"E197")}),-1.0]])]});
            var Q1;
            Q1=makeQuery(id+"F0.imprint","IMPRINT",FACE,{"disambiguationData":[TD([[makeQuery(id+"F0.imprint","IMPRINT",EDGE,{"derivedFrom":sQuery(id+"F0.wireOp",EDGE,"E0")}),-1.0]])]});
            var Q2;
            Q2=makeQuery(id+"F0.imprint","IMPRINT",FACE,{"disambiguationData":[TD([[makeQuery(id+"F0.imprint","IMPRINT",EDGE,{"derivedFrom":sQuery(id+"F0.wireOp",EDGE,"E149")}),-1.0]])]});
            extrude(context, id + "F1", {"entities" : qUnion([Q0, Q1, Q2]), "depth" : 1.8 * mm, "offsetDistance" : 25 * mm});
        }
        {
            var Q0;
            Q0=makeQuery(id+"F1.opExtrude","SWEPT_BODY",BODY,{"disambiguationData":[OSD([sQuery(id+"F0.wireOp",EDGE,"E0"),sQuery(id+"F0.wireOp",EDGE,"E1"),sQuery(id+"F0.wireOp",EDGE,"E2"),sQuery(id+"F0.wireOp",EDGE,"E3"),sQuery(id+"F0.wireOp",EDGE,"E4"),sQuery(id+"F0.wireOp",EDGE,"E5"),sQuery(id+"F0.wireOp",EDGE,"E6"),sQuery(id+"F0.wireOp",EDGE,"E7"),sQuery(id+"F0.wireOp",EDGE,"E8"),sQuery(id+"F0.wireOp",EDGE,"E9"),sQuery(id+"F0.wireOp",EDGE,"E10"),sQuery(id+"F0.wireOp",EDGE,"E11"),sQuery(id+"F0.wireOp",EDGE,"E12"),sQuery(id+"F0.wireOp",EDGE,"E13"),sQuery(id+"F0.wireOp",EDGE,"E14"),sQuery(id+"F0.wireOp",EDGE,"E15"),sQuery(id+"F0.wireOp",EDGE,"E16"),sQuery(id+"F0.wireOp",EDGE,"E17"),sQuery(id+"F0.wireOp",EDGE,"E18"),sQuery(id+"F0.wireOp",EDGE,"E19"),sQuery(id+"F0.wireOp",EDGE,"E20"),sQuery(id+"F0.wireOp",EDGE,"E21"),sQuery(id+"F0.wireOp",EDGE,"E22"),sQuery(id+"F0.wireOp",EDGE,"E23"),sQuery(id+"F0.wireOp",EDGE,"E24"),sQuery(id+"F0.wireOp",EDGE,"E25"),sQuery(id+"F0.wireOp",EDGE,"E26"),sQuery(id+"F0.wireOp",EDGE,"E27"),sQuery(id+"F0.wireOp",EDGE,"E28"),sQuery(id+"F0.wireOp",EDGE,"E29"),sQuery(id+"F0.wireOp",EDGE,"E30"),sQuery(id+"F0.wireOp",EDGE,"E31"),sQuery(id+"F0.wireOp",EDGE,"E32"),sQuery(id+"F0.wireOp",EDGE,"E33"),sQuery(id+"F0.wireOp",EDGE,"E34"),sQuery(id+"F0.wireOp",EDGE,"E35"),sQuery(id+"F0.wireOp",EDGE,"E36"),sQuery(id+"F0.wireOp",EDGE,"E37"),sQuery(id+"F0.wireOp",EDGE,"E38"),sQuery(id+"F0.wireOp",EDGE,"E39"),sQuery(id+"F0.wireOp",EDGE,"E40"),sQuery(id+"F0.wireOp",EDGE,"E41"),sQuery(id+"F0.wireOp",EDGE,"E42"),sQuery(id+"F0.wireOp",EDGE,"E43"),sQuery(id+"F0.wireOp",EDGE,"E44"),sQuery(id+"F0.wireOp",EDGE,"E45"),sQuery(id+"F0.wireOp",EDGE,"E46"),sQuery(id+"F0.wireOp",EDGE,"E47"),sQuery(id+"F0.wireOp",EDGE,"E48"),sQuery(id+"F0.wireOp",EDGE,"E49"),sQuery(id+"F0.wireOp",EDGE,"E50"),sQuery(id+"F0.wireOp",EDGE,"E51"),sQuery(id+"F0.wireOp",EDGE,"E52"),sQuery(id+"F0.wireOp",EDGE,"E53"),sQuery(id+"F0.wireOp",EDGE,"E54"),sQuery(id+"F0.wireOp",EDGE,"E55"),sQuery(id+"F0.wireOp",EDGE,"E56"),sQuery(id+"F0.wireOp",EDGE,"E57"),sQuery(id+"F0.wireOp",EDGE,"E58"),sQuery(id+"F0.wireOp",EDGE,"E59"),sQuery(id+"F0.wireOp",EDGE,"E60"),sQuery(id+"F0.wireOp",EDGE,"E61"),sQuery(id+"F0.wireOp",EDGE,"E62"),sQuery(id+"F0.wireOp",EDGE,"E63"),sQuery(id+"F0.wireOp",EDGE,"E64"),sQuery(id+"F0.wireOp",EDGE,"E65"),sQuery(id+"F0.wireOp",EDGE,"E66"),sQuery(id+"F0.wireOp",EDGE,"E67"),sQuery(id+"F0.wireOp",EDGE,"E68"),sQuery(id+"F0.wireOp",EDGE,"E69"),sQuery(id+"F0.wireOp",EDGE,"E70"),sQuery(id+"F0.wireOp",EDGE,"E71"),sQuery(id+"F0.wireOp",EDGE,"E72"),sQuery(id+"F0.wireOp",EDGE,"E73"),sQuery(id+"F0.wireOp",EDGE,"E74"),sQuery(id+"F0.wireOp",EDGE,"E75"),sQuery(id+"F0.wireOp",EDGE,"E76"),sQuery(id+"F0.wireOp",EDGE,"E77"),sQuery(id+"F0.wireOp",EDGE,"E78"),sQuery(id+"F0.wireOp",EDGE,"E79"),sQuery(id+"F0.wireOp",EDGE,"E80"),sQuery(id+"F0.wireOp",EDGE,"E81"),sQuery(id+"F0.wireOp",EDGE,"E82"),sQuery(id+"F0.wireOp",EDGE,"E83"),sQuery(id+"F0.wireOp",EDGE,"E84"),sQuery(id+"F0.wireOp",EDGE,"E85"),sQuery(id+"F0.wireOp",EDGE,"E86"),sQuery(id+"F0.wireOp",EDGE,"E87"),sQuery(id+"F0.wireOp",EDGE,"E88"),sQuery(id+"F0.wireOp",EDGE,"E89"),sQuery(id+"F0.wireOp",EDGE,"E90"),sQuery(id+"F0.wireOp",EDGE,"E91"),sQuery(id+"F0.wireOp",EDGE,"E92"),sQuery(id+"F0.wireOp",EDGE,"E93"),sQuery(id+"F0.wireOp",EDGE,"E94"),sQuery(id+"F0.wireOp",EDGE,"E95"),sQuery(id+"F0.wireOp",EDGE,"E96"),sQuery(id+"F0.wireOp",EDGE,"E97"),sQuery(id+"F0.wireOp",EDGE,"E98"),sQuery(id+"F0.wireOp",EDGE,"E99"),sQuery(id+"F0.wireOp",EDGE,"E100"),sQuery(id+"F0.wireOp",EDGE,"E101"),sQuery(id+"F0.wireOp",EDGE,"E102"),sQuery(id+"F0.wireOp",EDGE,"E103"),sQuery(id+"F0.wireOp",EDGE,"E104"),sQuery(id+"F0.wireOp",EDGE,"E105"),sQuery(id+"F0.wireOp",EDGE,"E106"),sQuery(id+"F0.wireOp",EDGE,"E107"),sQuery(id+"F0.wireOp",EDGE,"E108"),sQuery(id+"F0.wireOp",EDGE,"E109"),sQuery(id+"F0.wireOp",EDGE,"E110"),sQuery(id+"F0.wireOp",EDGE,"E111"),sQuery(id+"F0.wireOp",EDGE,"E112"),sQuery(id+"F0.wireOp",EDGE,"E113"),sQuery(id+"F0.wireOp",EDGE,"E114"),sQuery(id+"F0.wireOp",EDGE,"E115"),sQuery(id+"F0.wireOp",EDGE,"E116"),sQuery(id+"F0.wireOp",EDGE,"E117"),sQuery(id+"F0.wireOp",EDGE,"E118"),sQuery(id+"F0.wireOp",EDGE,"E119"),sQuery(id+"F0.wireOp",EDGE,"E120"),sQuery(id+"F0.wireOp",EDGE,"E121"),sQuery(id+"F0.wireOp",EDGE,"E122"),sQuery(id+"F0.wireOp",EDGE,"E123"),sQuery(id+"F0.wireOp",EDGE,"E124"),sQuery(id+"F0.wireOp",EDGE,"E125"),sQuery(id+"F0.wireOp",EDGE,"E126"),sQuery(id+"F0.wireOp",EDGE,"E127"),sQuery(id+"F0.wireOp",EDGE,"E128"),sQuery(id+"F0.wireOp",EDGE,"E129"),sQuery(id+"F0.wireOp",EDGE,"E130"),sQuery(id+"F0.wireOp",EDGE,"E131"),sQuery(id+"F0.wireOp",EDGE,"E132"),sQuery(id+"F0.wireOp",EDGE,"E133"),sQuery(id+"F0.wireOp",EDGE,"E134"),sQuery(id+"F0.wireOp",EDGE,"E135"),sQuery(id+"F0.wireOp",EDGE,"E136"),sQuery(id+"F0.wireOp",EDGE,"E137"),sQuery(id+"F0.wireOp",EDGE,"E138"),sQuery(id+"F0.wireOp",EDGE,"E139"),sQuery(id+"F0.wireOp",EDGE,"E140"),sQuery(id+"F0.wireOp",EDGE,"E141"),sQuery(id+"F0.wireOp",EDGE,"E142"),sQuery(id+"F0.wireOp",EDGE,"E143"),sQuery(id+"F0.wireOp",EDGE,"E144"),sQuery(id+"F0.wireOp",EDGE,"E145"),sQuery(id+"F0.wireOp",EDGE,"E146"),sQuery(id+"F0.wireOp",EDGE,"E147"),sQuery(id+"F0.wireOp",EDGE,"E148")])]});
            var Q1;
            Q1=makeQuery(id+"F1.opExtrude","SWEPT_BODY",BODY,{"disambiguationData":[OSD([sQuery(id+"F0.wireOp",EDGE,"E149"),sQuery(id+"F0.wireOp",EDGE,"E150"),sQuery(id+"F0.wireOp",EDGE,"E151"),sQuery(id+"F0.wireOp",EDGE,"E152"),sQuery(id+"F0.wireOp",EDGE,"E153"),sQuery(id+"F0.wireOp",EDGE,"E154"),sQuery(id+"F0.wireOp",EDGE,"E155"),sQuery(id+"F0.wireOp",EDGE,"E156"),sQuery(id+"F0.wireOp",EDGE,"E157"),sQuery(id+"F0.wireOp",EDGE,"E158"),sQuery(id+"F0.wireOp",EDGE,"E159"),sQuery(id+"F0.wireOp",EDGE,"E160"),sQuery(id+"F0.wireOp",EDGE,"E161"),sQuery(id+"F0.wireOp",EDGE,"E162"),sQuery(id+"F0.wireOp",EDGE,"E163"),sQuery(id+"F0.wireOp",EDGE,"E164"),sQuery(id+"F0.wireOp",EDGE,"E165"),sQuery(id+"F0.wireOp",EDGE,"E166"),sQuery(id+"F0.wireOp",EDGE,"E167"),sQuery(id+"F0.wireOp",EDGE,"E168"),sQuery(id+"F0.wireOp",EDGE,"E169"),sQuery(id+"F0.wireOp",EDGE,"E170"),sQuery(id+"F0.wireOp",EDGE,"E171"),sQuery(id+"F0.wireOp",EDGE,"E172"),sQuery(id+"F0.wireOp",EDGE,"E173"),sQuery(id+"F0.wireOp",EDGE,"E174"),sQuery(id+"F0.wireOp",EDGE,"E175"),sQuery(id+"F0.wireOp",EDGE,"E176"),sQuery(id+"F0.wireOp",EDGE,"E177"),sQuery(id+"F0.wireOp",EDGE,"E178"),sQuery(id+"F0.wireOp",EDGE,"E179"),sQuery(id+"F0.wireOp",EDGE,"E180"),sQuery(id+"F0.wireOp",EDGE,"E181"),sQuery(id+"F0.wireOp",EDGE,"E182"),sQuery(id+"F0.wireOp",EDGE,"E183"),sQuery(id+"F0.wireOp",EDGE,"E184"),sQuery(id+"F0.wireOp",EDGE,"E185"),sQuery(id+"F0.wireOp",EDGE,"E186"),sQuery(id+"F0.wireOp",EDGE,"E187"),sQuery(id+"F0.wireOp",EDGE,"E188"),sQuery(id+"F0.wireOp",EDGE,"E189"),sQuery(id+"F0.wireOp",EDGE,"E190"),sQuery(id+"F0.wireOp",EDGE,"E191"),sQuery(id+"F0.wireOp",EDGE,"E192"),sQuery(id+"F0.wireOp",EDGE,"E193"),sQuery(id+"F0.wireOp",EDGE,"E194"),sQuery(id+"F0.wireOp",EDGE,"E195"),sQuery(id+"F0.wireOp",EDGE,"E196")])]});
            var Q2;
            Q2=makeQuery(id+"F1.opExtrude","SWEPT_BODY",BODY,{"disambiguationData":[OSD([sQuery(id+"F0.wireOp",EDGE,"E197"),sQuery(id+"F0.wireOp",EDGE,"E198"),sQuery(id+"F0.wireOp",EDGE,"E199"),sQuery(id+"F0.wireOp",EDGE,"E200"),sQuery(id+"F0.wireOp",EDGE,"E201"),sQuery(id+"F0.wireOp",EDGE,"E202"),sQuery(id+"F0.wireOp",EDGE,"E203"),sQuery(id+"F0.wireOp",EDGE,"E204"),sQuery(id+"F0.wireOp",EDGE,"E205"),sQuery(id+"F0.wireOp",EDGE,"E206"),sQuery(id+"F0.wireOp",EDGE,"E207"),sQuery(id+"F0.wireOp",EDGE,"E208"),sQuery(id+"F0.wireOp",EDGE,"E209"),sQuery(id+"F0.wireOp",EDGE,"E210"),sQuery(id+"F0.wireOp",EDGE,"E211"),sQuery(id+"F0.wireOp",EDGE,"E212"),sQuery(id+"F0.wireOp",EDGE,"E213"),sQuery(id+"F0.wireOp",EDGE,"E214"),sQuery(id+"F0.wireOp",EDGE,"E215"),sQuery(id+"F0.wireOp",EDGE,"E216"),sQuery(id+"F0.wireOp",EDGE,"E217"),sQuery(id+"F0.wireOp",EDGE,"E218"),sQuery(id+"F0.wireOp",EDGE,"E219"),sQuery(id+"F0.wireOp",EDGE,"E220"),sQuery(id+"F0.wireOp",EDGE,"E221"),sQuery(id+"F0.wireOp",EDGE,"E222"),sQuery(id+"F0.wireOp",EDGE,"E223"),sQuery(id+"F0.wireOp",EDGE,"E224"),sQuery(id+"F0.wireOp",EDGE,"E225"),sQuery(id+"F0.wireOp",EDGE,"E226"),sQuery(id+"F0.wireOp",EDGE,"E227"),sQuery(id+"F0.wireOp",EDGE,"E228"),sQuery(id+"F0.wireOp",EDGE,"E229"),sQuery(id+"F0.wireOp",EDGE,"E230"),sQuery(id+"F0.wireOp",EDGE,"E231"),sQuery(id+"F0.wireOp",EDGE,"E232"),sQuery(id+"F0.wireOp",EDGE,"E233"),sQuery(id+"F0.wireOp",EDGE,"E234"),sQuery(id+"F0.wireOp",EDGE,"E235"),sQuery(id+"F0.wireOp",EDGE,"E236"),sQuery(id+"F0.wireOp",EDGE,"E237"),sQuery(id+"F0.wireOp",EDGE,"E238"),sQuery(id+"F0.wireOp",EDGE,"E239"),sQuery(id+"F0.wireOp",EDGE,"E240"),sQuery(id+"F0.wireOp",EDGE,"E241"),sQuery(id+"F0.wireOp",EDGE,"E242"),sQuery(id+"F0.wireOp",EDGE,"E243"),sQuery(id+"F0.wireOp",EDGE,"E244"),sQuery(id+"F0.wireOp",EDGE,"E245"),sQuery(id+"F0.wireOp",EDGE,"E246"),sQuery(id+"F0.wireOp",EDGE,"E247"),sQuery(id+"F0.wireOp",EDGE,"E248"),sQuery(id+"F0.wireOp",EDGE,"E249"),sQuery(id+"F0.wireOp",EDGE,"E250"),sQuery(id+"F0.wireOp",EDGE,"E251"),sQuery(id+"F0.wireOp",EDGE,"E252"),sQuery(id+"F0.wireOp",EDGE,"E253"),sQuery(id+"F0.wireOp",EDGE,"E254"),sQuery(id+"F0.wireOp",EDGE,"E255"),sQuery(id+"F0.wireOp",EDGE,"E256"),sQuery(id+"F0.wireOp",EDGE,"E257"),sQuery(id+"F0.wireOp",EDGE,"E258"),sQuery(id+"F0.wireOp",EDGE,"E259"),sQuery(id+"F0.wireOp",EDGE,"E260"),sQuery(id+"F0.wireOp",EDGE,"E261"),sQuery(id+"F0.wireOp",EDGE,"E262"),sQuery(id+"F0.wireOp",EDGE,"E263"),sQuery(id+"F0.wireOp",EDGE,"E264"),sQuery(id+"F0.wireOp",EDGE,"E265"),sQuery(id+"F0.wireOp",EDGE,"E266"),sQuery(id+"F0.wireOp",EDGE,"E267"),sQuery(id+"F0.wireOp",EDGE,"E268"),sQuery(id+"F0.wireOp",EDGE,"E269"),sQuery(id+"F0.wireOp",EDGE,"E270"),sQuery(id+"F0.wireOp",EDGE,"E271"),sQuery(id+"F0.wireOp",EDGE,"E272"),sQuery(id+"F0.wireOp",EDGE,"E273"),sQuery(id+"F0.wireOp",EDGE,"E274"),sQuery(id+"F0.wireOp",EDGE,"E275"),sQuery(id+"F0.wireOp",EDGE,"E276"),sQuery(id+"F0.wireOp",EDGE,"E277"),sQuery(id+"F0.wireOp",EDGE,"E278"),sQuery(id+"F0.wireOp",EDGE,"E279"),sQuery(id+"F0.wireOp",EDGE,"E280"),sQuery(id+"F0.wireOp",EDGE,"E281"),sQuery(id+"F0.wireOp",EDGE,"E282"),sQuery(id+"F0.wireOp",EDGE,"E283"),sQuery(id+"F0.wireOp",EDGE,"E284"),sQuery(id+"F0.wireOp",EDGE,"E285"),sQuery(id+"F0.wireOp",EDGE,"E286"),sQuery(id+"F0.wireOp",EDGE,"E287"),sQuery(id+"F0.wireOp",EDGE,"E288"),sQuery(id+"F0.wireOp",EDGE,"E289"),sQuery(id+"F0.wireOp",EDGE,"E290"),sQuery(id+"F0.wireOp",EDGE,"E291"),sQuery(id+"F0.wireOp",EDGE,"E292"),sQuery(id+"F0.wireOp",EDGE,"E293"),sQuery(id+"F0.wireOp",EDGE,"E294"),sQuery(id+"F0.wireOp",EDGE,"E295"),sQuery(id+"F0.wireOp",EDGE,"E296"),sQuery(id+"F0.wireOp",EDGE,"E297"),sQuery(id+"F0.wireOp",EDGE,"E298"),sQuery(id+"F0.wireOp",EDGE,"E299"),sQuery(id+"F0.wireOp",EDGE,"E300"),sQuery(id+"F0.wireOp",EDGE,"E301"),sQuery(id+"F0.wireOp",EDGE,"E302"),sQuery(id+"F0.wireOp",EDGE,"E303"),sQuery(id+"F0.wireOp",EDGE,"E304"),sQuery(id+"F0.wireOp",EDGE,"E305"),sQuery(id+"F0.wireOp",EDGE,"E306"),sQuery(id+"F0.wireOp",EDGE,"E307"),sQuery(id+"F0.wireOp",EDGE,"E308"),sQuery(id+"F0.wireOp",EDGE,"E309"),sQuery(id+"F0.wireOp",EDGE,"E310")])]});
            var Q3;
            Q3=makeQuery(id+"F1.opExtrude","CAP_VERTEX",VERTEX,{"disambiguationData":[OSD([sQuery(id+"F0.wireOp",EDGE,"E138"),sQuery(id+"F0.wireOp",EDGE,"E139")])],"isStart":false});
            transform(context, id + "F2", {"entities" : qUnion([Q0, Q1, Q2]), "transformType" : TransformType.SCALE_UNIFORMLY, "scale" : 10, "scalePoint" : qUnion([Q3]), "makeCopy" : false});
        }
    });
